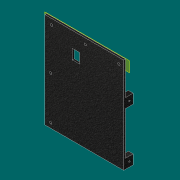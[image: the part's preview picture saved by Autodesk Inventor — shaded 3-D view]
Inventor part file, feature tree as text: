
AUTODESK INVENTOR PART (.ipt)
format: ipt  version: 2019 (Build 230136000, 136)  size: 216,064 bytes
history: native  units: mm
features: reference x17, sketch x13, extrude x11, other x3, plane x1
ambient origin geometry x8: Origin, YZ Plane, XZ Plane, XY Plane, X Axis, Y Axis, Z Axis, Center Point
bodies: Solid1 (feature_tree)
feature tree (45):
  plane  "Work Plane1"
  extrude  "Extrusion1"  Depth=8.0mm
  sketch  "Sketch2"  dims[d4=10.0mm d6=1.5mm]
  sketch  "Sketch3"  dims[d7=5.0mm d8=0.0mm d9=8.0mm]
  extrude  "Extrusion2"  Depth=10.0mm
  extrude  "Extrusion3"  Depth=8.0mm
  extrude  "Extrusion4"  Depth=10.0mm
  extrude  "Extrusion5"  Depth=10.0mm
  extrude  "Extrusion6"  Depth=8.0mm
  extrude  "Extrusion7"  Depth=5.0mm
  extrude  "Extrusion8"  Depth=5.0mm
  extrude  "Extrusion9"  Depth=10.0mm
  extrude  "Extrusion10"  Depth=5.0mm TaperAngle=0.0deg
  extrude  "Extrusion11"  Depth=8.0mm
  sketch  "Sketch1"  dims[d0=2.0mm d1=0.0mm d3=8.0mm]
  reference  "Reference1"
  reference  "Reference2"
  reference  "Reference3"
  reference  "Reference4"
  reference  "Reference5"
  reference  "Reference6"
  reference  "Reference7"
  reference  "Reference8"
  reference  "Reference9"
  sketch  "Sketch4"  dims[d10=10.0mm d12=1.5mm]
  reference  "Reference10"
  reference  "Reference11"
  reference  "Reference12"
  reference  "Reference13"
  sketch  "Sketch5"  dims[d13=5.0mm d14=0.0mm d15=10.0mm]
  sketch  "Sketch6"  dims[d16=8.0mm d18=1.5mm]
  sketch  "Sketch7"  dims[d19=5.0mm d20=0.0mm d22=1.5mm]
  reference  "Reference14"
  sketch  "Sketch8"  dims[d25=4.0mm d26=5.0mm]
  sketch  "Sketch9"  dims[d27=8.0mm d28=10.0mm]
  reference  "Reference15"
  reference  "Reference16"
  reference  "Reference17"
  sketch  "Sketch10"  dims[d29=8.0mm d30=5.0mm d31=0.0mm]
  sketch  "Sketch11"  dims[d32=5.0mm d33=0.0mm d35=8.0mm]
  sketch  "Sketch12"  dims[d36=10.0mm]
  sketch  "Sketch13"  dims[d38=1.5mm d39=5.0mm d40=0.0mm d41=10.0mm d42=8.0mm d43=0.0mm d44=5.0mm d45=10.0mm d46=5.0mm d47=10.0mm d48=8.0mm d49=0.0mm d51=1.5mm d52=5.0mm d53=0.0mm d54=2.5mm d55=2.5mm d56=2.5mm d57=2.5mm d58=2.5mm d59=2.0mm d60=0.0mm]
  other  "Ensamblaje Reloj LCD 16x2.iam"
  other  "Before:1"
  other  "Down:1"
